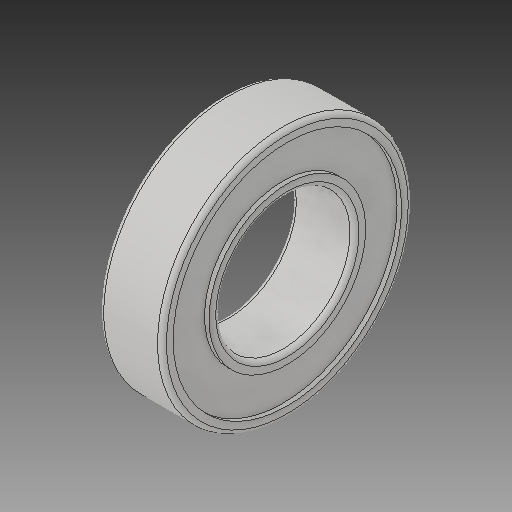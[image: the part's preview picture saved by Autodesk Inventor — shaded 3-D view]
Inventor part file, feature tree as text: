
AUTODESK INVENTOR PART (.ipt)
format: ipt  version: 2017 (Build 210142000, 142)  size: 181,760 bytes
history: native  units: in
note: dims shown in document units (in); Inventor stores cm internally (conversion verified against a paired STEP export)
features: fillet x1
ambient origin geometry x8: Origin, YZ Plane, XZ Plane, XY Plane, X Axis, Y Axis, Z Axis, Center Point
bodies: Solid1 (feature_tree)
feature tree (1):
  fillet  "Fillet1"  [1 undecoded]
note: 1 required parameter value undecoded (feature->parameter linkage not recoverable at this tier; creation-order binding heuristic only, values carry confidence <= 0.55)
